# Revit family: IS_BlendCurve_T3753_BIM_NL
name_source: partatom
category: Plumbing Fixtures
units: mm (PartAtom-declared; Revit-internal decimal feet)

## family parameters
Always vertical = No
Cut with Voids When Loaded = No
OmniClass Number = 23.45.05.14.27
OmniClass Title = Bidets
Part Type = Normal
Room Calculation Point = No
Round Connector Dimension = Use Diameter
Shared = No
Work Plane-Based = No

## types (1)
- T375301 - Blend Curve Back to Wall Bidet, Hidden Fixation, Glossy White
    Accesoires = https://www.idealstandard.nl
    Accessories = https://www.idealstandard.nl
    Afmetingen = 356 x 560 x 400 mm
    Afwerking = Wit
    AreaUnits = millimetres
    Artikelnummer = T375301
    Artikelomschrijving = Stand-Bidet Blend Curve, 1 Hl., 355x560x400mm, Weiß
    Artikelreferentie = Stand-Bidet Blend Curve, 1 Hl., 355x560x400mm, Weiß
    Auteur = Ideal Standard
    BIMObjectName = IS_IdealStandard_Bidets_BlendCurve_T3753
    BIMobject category = Bidets
    BIMobject category code = sanitary-bidets
    BIMobject main category = Sanitary
    BIMobject main category code = sanitary
    BarCode = 8014140468332
    Barcode = 8014140468332
    Beschrijvinggarantie = Herstellergarantie
    Bestanddelen = Stand-Bidet Blend Curve, 1 Hl., 355x560x400mm, Weiß
    BidetMounting = Back to Wall
    BimObjectNaam = IS_IdealStandard_Bidets_BlendCurve_T3753
    Brand = Ideal Standard
    Brand url = https://www.idealstandard.nl
    Breedte = 0
    BrutoGewicht = 0
    Color = White
    ConnectionType = Plumbing
    Cost = 0 $
    CurrencyUnit = €
    CurrentRevision = 1
    Date of publishing = 30/04/2021
    Description = Blend Curve Back to Wall Bidet, Hidden Fixation, Glossy White
    Diepte = 560 mm
    DurationUnit = Years
    DuurEenheid = Jahre
    Edition number = 1
    Eigenschappen = Stand-Bidet Blend Curve, 1 Hl., 355x560x400mm, Weiß
    ExpectedLife = 99
    Features = Back to Wall Bidet with Hidden Fixation in Glossy White Finish
    Finish = White
    GTIN code = https://8014140468332
    Garantieunits = Jahre
    GemaaktOp = 26/04/2021
    Help = https://www.idealstandard.nl
    Hoogte = 400.022257730365
    Hulp = https://www.idealstandard.nl
    IFC Classification = Sanitary Terminal
    IfcExportAs = IfcSanitaryTerminalType
    IfcExportType = BIDET
    Installatieinstructies = https://www.idealstandard.nl
    Installation instructions = https://www.idealstandard.nl
    InstallationInstructions = https://www.idealstandard.nl
    Kleur = Weiß
    Lengte = 0 mm  [stored 0 ft]
    LinearUnits = millimetres
    MainColor = White
    MaintenanceInformation = https://www.idealstandard.nl
    Manufacturer = Ideal Standard Nederland BV
    Manufacturer name = Ideal Standard
    ManufacturerURL = https://www.idealstandard.nl
    Masterformat 2014 Code = 22 41 13.19
    Masterformat 2014 Description = Residential Bidets
    Materiaal = Vuurvaste klei
    Material = Fine Fireclay
    Material main = Fireclay
    Merk = Ideal Standard
    Model = T375301
    ModelNumber = T375301
    ModelReference = Blend Curve Back to Wall Bidet, Hidden Fixation, Glossy White
    Montageinstuctie = https://www.idealstandard.nl
    NBS Reference Code = 45-35-70/320
    NBS Reference Description = Bidets
    Name = Bidets_BlendCurve_T3753_IdealStandard
    NettWeight = 23.9
    Nettogewicht = 23.9
    NominalDepth = 560 mm
    NominalHeight = 400 mm
    NominalWidth = 356 mm
    Normen = Bidets_BlendCurve_T3753_IdealStandard
    OmniClass Code = 23-31 23 00
    OmniClass Description = Bidets
    OppervlakteEenheid = Millimeter
    Overloop = 0 mm  [stored 0 ft]
    PredefinedType = Bidets
    Product Guid = 7bd5273c-1318-41f6-96f1-4a484af4b8db
    Product SKU = T3753
    Product certification = https://www.idealstandard.nl
    Product data url = https://bimobject.com
    Product family = Blend Cube
    Product group = Bidet
    Product name = Blend Curve Back to Wall Bidet
    Product url = https://www.idealstandard.nl
    ProductInformation = https://www.idealstandard.nl
    ProductSoort = Sanitärartikel
    Productinformatie = https://www.idealstandard.nl
    QR code = http://bimobject.com
    Referentie = T375301
    Revisie = 1
    SeatHasCover = No
    Shape = Sculpture
    Size = 356 x 560 x 400 mm
    Space = Internal
    SpareParts = https://www.idealstandard.nl
    Technical description = https://www.idealstandard.nl
    Telefoonnummer = 0049 228 5210
    Typeconnectie = Installation
    UNSPSC Code = 30181502
    URL = https://www.idealstandard.nl
    Uniclass 1.4 Code = L7215
    Uniclass 1.4 Description = Bidets
    Uniclass 2.0 Code = PR-35-06-11
    Uniclass 2.0 Description = Bidets
    Uniclass 2015 Code = Pr_40_20_06_11
    Uniclass 2015 Name = Bidets
    Uniclass2015Version = v1.20
    Uniformat II Code = D2010
    Uniformat II Description = Plumbing Fixtures
    Urlproducent = https://www.idealstandard.nl
    ValutaEenheid = €
    Versie = 1
    Version = 1
    Vervangingskosten = 0
    VolumeUnits = Liters
    Volumeunits = Liter
    Vorm = Skulptur
    WRASURL = https://www.wrasapprovals.co.uk
    WarrantyDescription = Manufacturer Warranty
    WarrantyDurationParts = 99
    WarrantyDurationUnit = Years
    Wisselstukken = https://www.idealstandard.nl
    Youtube clip = https://www.youtube.com

note: [stored X ft] marks values corroborated as IEEE doubles in the binary element streams (Revit-internal decimal feet)

## geometry (parser evidence)
native form markers: Blend x31, Sweep x3
no freeform markers — native parametric forms only
